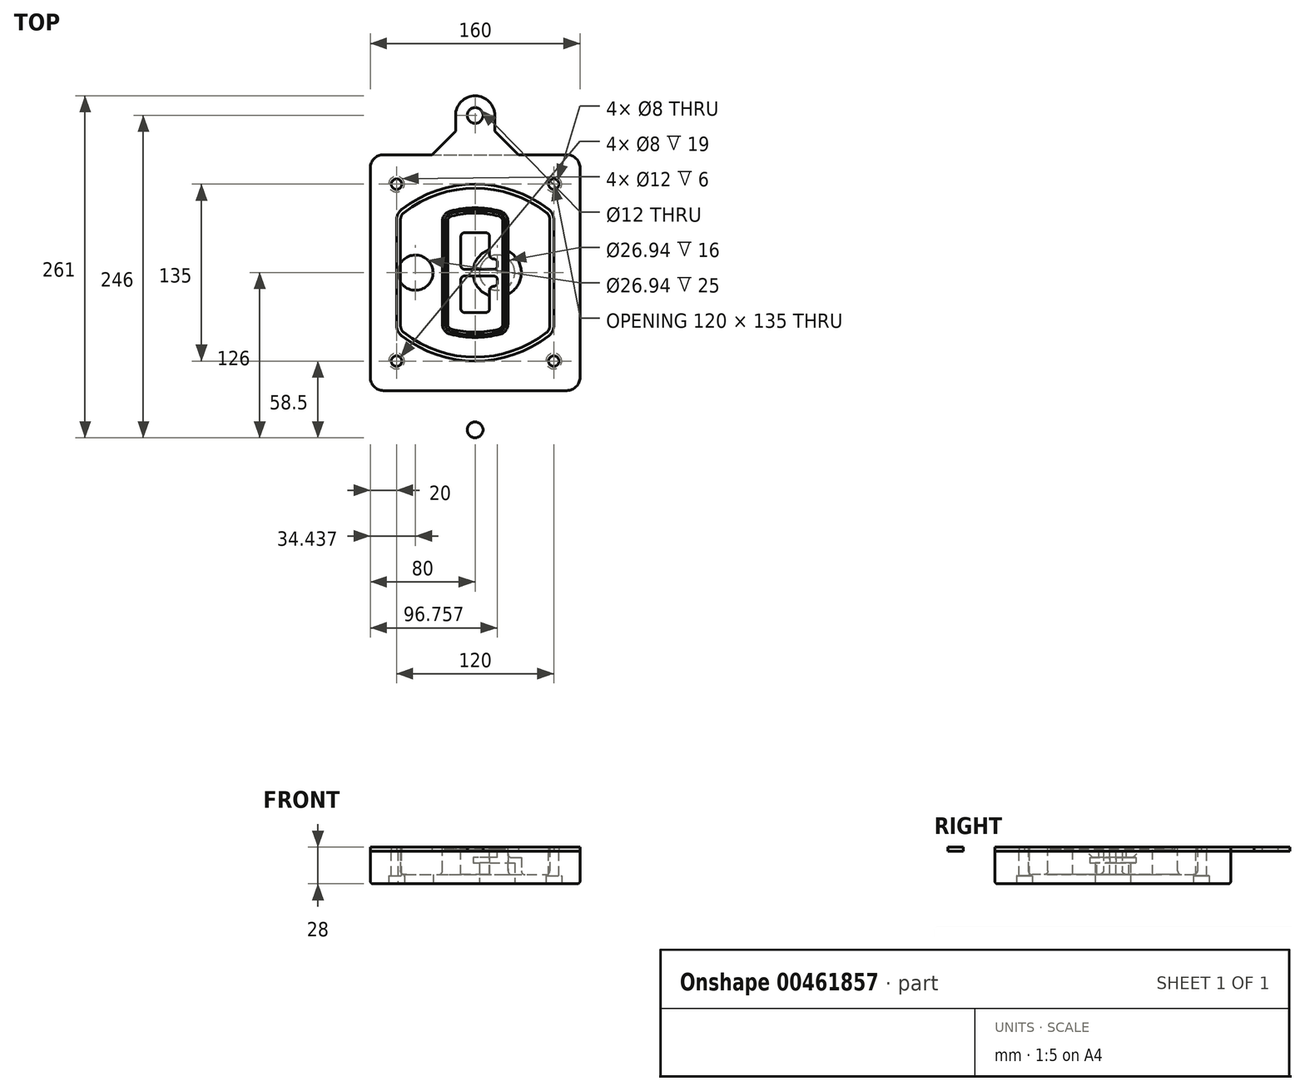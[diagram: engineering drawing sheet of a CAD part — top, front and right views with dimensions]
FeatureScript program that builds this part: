
annotation { "Feature Type Name" : "Feature", "Feature Type Description" : "" }
export const myFeature = defineFeature(function(context is Context, id is Id, definition is map)
    precondition{}
    {
        {
            var Q0;
            Q0=qCreatedBy(makeId("Top.planeOp"),FACE);
            var sketch = newSketch(context, id + "F0", { "sketchPlane" : qUnion([Q0])});
            skPoint(sketch, "E0.rect.middle", {"position": v(0, 0) * mm});
            skLineSegment(sketch, "E1.bottom", {"start": v(-70, -90) * mm, "end": v(70, -90) * mm});
            skLineSegment(sketch, "E1.top", {"start": v(-70, 90) * mm, "end": v(70, 90) * mm});
            skLineSegment(sketch, "E1.left", {"start": v(-80, -80) * mm, "end": v(-80, 80) * mm});
            skLineSegment(sketch, "E1.right", {"start": v(80, -80) * mm, "end": v(80, 80) * mm});
            skLineSegment(sketch, "E2", {"start": v(-80, 90) * mm, "end": v(80, -90) * mm, "construction": true});
            skLineSegment(sketch, "E3", {"start": v(80, 90) * mm, "end": v(-80, -90) * mm, "construction": true});
            skCircle(sketch, "E4", {"center": v(-60, 67.5) * mm, "radius": 4 * mm});
            skCircle(sketch, "E5", {"center": v(60, 67.5) * mm, "radius": 4 * mm});
            skCircle(sketch, "E6", {"center": v(60, -67.5) * mm, "radius": 4 * mm});
            skCircle(sketch, "E7", {"center": v(-60, -67.5) * mm, "radius": 4 * mm});
            skLineSegment(sketch, "E8", {"start": v(-60, 67.5) * mm, "end": v(60, 67.5) * mm, "construction": true});
            skLineSegment(sketch, "E9", {"start": v(60, 67.5) * mm, "end": v(60, -67.5) * mm, "construction": true});
            skLineSegment(sketch, "E10", {"start": v(60, -67.5) * mm, "end": v(-60, -67.5) * mm, "construction": true});
            skLineSegment(sketch, "E11", {"start": v(-60, -67.5) * mm, "end": v(-60, 67.5) * mm, "construction": true});
            skLineSegment(sketch, "E12", {"start": v(-60, 40.3) * mm, "end": v(-60, -40.3) * mm});
            skLineSegment(sketch, "E13", {"start": v(60, 40.3) * mm, "end": v(60, -40.3) * mm});
            skArc(sketch, "E14", {"start": v(56.15, 48.18) * mm, "mid": v(0, 67.5) * mm, "end": v(-56.15, 48.18) * mm});
            skArc(sketch, "E15", {"start": v(-56.15, -48.18) * mm, "mid": v(0, -67.5) * mm, "end": v(56.15, -48.18) * mm});
            skLineSegment(sketch, "E16", {"start": v(-60, 0) * mm, "end": v(60, 0) * mm, "construction": true});
            skPoint(sketch, "E17.visualSharp", {"position": v(-60, -45) * mm});
            skArc(sketch, "E17.filletArc", {"start": v(-60, -40.3) * mm, "mid": v(-58.99, -44.68) * mm, "end": v(-56.15, -48.18) * mm});
            skPoint(sketch, "E18.visualSharp", {"position": v(-60, 45) * mm});
            skArc(sketch, "E18.filletArc", {"start": v(-56.15, 48.18) * mm, "mid": v(-58.99, 44.68) * mm, "end": v(-60, 40.3) * mm});
            skPoint(sketch, "E19.visualSharp", {"position": v(60, 45) * mm});
            skArc(sketch, "E19.filletArc", {"start": v(60, 40.3) * mm, "mid": v(58.99, 44.68) * mm, "end": v(56.15, 48.18) * mm});
            skPoint(sketch, "E20.visualSharp", {"position": v(60, -45) * mm});
            skArc(sketch, "E20.filletArc", {"start": v(56.15, -48.18) * mm, "mid": v(58.99, -44.68) * mm, "end": v(60, -40.3) * mm});
            skPoint(sketch, "E21.visualSharp", {"position": v(-80, 90) * mm});
            skArc(sketch, "E21.filletArc", {"start": v(-70, 90) * mm, "mid": v(-77.07, 87.07) * mm, "end": v(-80, 80) * mm});
            skPoint(sketch, "E22.visualSharp", {"position": v(80, 90) * mm});
            skArc(sketch, "E22.filletArc", {"start": v(80, 80) * mm, "mid": v(77.07, 87.07) * mm, "end": v(70, 90) * mm});
            skPoint(sketch, "E23.visualSharp", {"position": v(80, -90) * mm});
            skArc(sketch, "E23.filletArc", {"start": v(70, -90) * mm, "mid": v(77.07, -87.07) * mm, "end": v(80, -80) * mm});
            skPoint(sketch, "E24.visualSharp", {"position": v(-80, -90) * mm});
            skArc(sketch, "E24.filletArc", {"start": v(-80, -80) * mm, "mid": v(-77.07, -87.07) * mm, "end": v(-70, -90) * mm});
            skArc(sketch, "E25.0", {"start": v(57, 40.3) * mm, "mid": v(56.3, 43.36) * mm, "end": v(54.3, 45.81) * mm});
            skLineSegment(sketch, "E25.1", {"start": v(57, 40.3) * mm, "end": v(57, -40.3) * mm});
            skArc(sketch, "E25.2", {"start": v(54.3, -45.81) * mm, "mid": v(56.3, -43.36) * mm, "end": v(57, -40.3) * mm});
            skArc(sketch, "E25.3", {"start": v(-54.3, -45.81) * mm, "mid": v(0, -64.5) * mm, "end": v(54.3, -45.81) * mm});
            skArc(sketch, "E25.4", {"start": v(-57, -40.3) * mm, "mid": v(-56.3, -43.36) * mm, "end": v(-54.3, -45.81) * mm});
            skArc(sketch, "E25.5", {"start": v(54.3, 45.81) * mm, "mid": v(0, 64.5) * mm, "end": v(-54.3, 45.81) * mm});
            skLineSegment(sketch, "E25.6", {"start": v(-57, 40.3) * mm, "end": v(-57, -40.3) * mm});
            skArc(sketch, "E25.7", {"start": v(-54.3, 45.81) * mm, "mid": v(-56.3, 43.36) * mm, "end": v(-57, 40.3) * mm});
            skArc(sketch, "E26.0", {"start": v(-58.62, 51.33) * mm, "mid": v(-62.58, 46.43) * mm, "end": v(-64, 40.3) * mm});
            skArc(sketch, "E26.1", {"start": v(58.62, 51.33) * mm, "mid": v(0, 71.5) * mm, "end": v(-58.62, 51.33) * mm});
            skArc(sketch, "E26.2", {"start": v(64, 40.3) * mm, "mid": v(62.58, 46.43) * mm, "end": v(58.62, 51.33) * mm});
            skLineSegment(sketch, "E26.3", {"start": v(64, 40.3) * mm, "end": v(64, -40.3) * mm});
            skArc(sketch, "E26.4", {"start": v(58.62, -51.33) * mm, "mid": v(62.58, -46.43) * mm, "end": v(64, -40.3) * mm});
            skLineSegment(sketch, "E26.5", {"start": v(-64, 40.3) * mm, "end": v(-64, -40.3) * mm});
            skArc(sketch, "E26.6", {"start": v(-58.62, -51.33) * mm, "mid": v(0, -71.5) * mm, "end": v(58.62, -51.33) * mm});
            skArc(sketch, "E26.7", {"start": v(-64, -40.3) * mm, "mid": v(-62.58, -46.43) * mm, "end": v(-58.62, -51.33) * mm});
            skSolve(sketch);
        }
        {
            var Q0;
            Q0=makeQuery(id+"F0.imprint","IMPRINT",FACE,{"disambiguationData":[TD([[makeQuery(id+"F0.imprint","IMPRINT",EDGE,{"derivedFrom":sQuery(id+"F0.wireOp",EDGE,"E1.bottom")}),1.0]])]});
            var Q1;
            Q1=makeQuery(id+"F0.imprint","IMPRINT",FACE,{"disambiguationData":[TD([[makeQuery(id+"F0.imprint","IMPRINT",EDGE,{"derivedFrom":sQuery(id+"F0.wireOp",EDGE,"E12")}),1.0]])]});
            var Q2;
            Q2=makeQuery(id+"F0.imprint","IMPRINT",FACE,{"disambiguationData":[TD([[makeQuery(id+"F0.imprint","IMPRINT",EDGE,{"derivedFrom":sQuery(id+"F0.wireOp",EDGE,"E25.0")}),1.0]])]});
            var Q3;
            Q3=makeQuery(id+"F0.imprint","IMPRINT",FACE,{"disambiguationData":[TD([[makeQuery(id+"F0.imprint","IMPRINT",EDGE,{"derivedFrom":sQuery(id+"F0.wireOp",EDGE,"E12")}),-1.0]])]});
            extrude(context, id + "F1", {"entities" : qUnion([Q0, Q1, Q2, Q3]), "oppositeDirection" : true, "depth" : 25 * mm});
        }
        {
            var Q0;
            Q0=makeQuery(id+"F0.imprint","IMPRINT",FACE,{"disambiguationData":[TD([[makeQuery(id+"F0.imprint","IMPRINT",EDGE,{"derivedFrom":sQuery(id+"F0.wireOp",EDGE,"E12")}),1.0]])]});
            extrude(context, id + "F2", {"entities" : qUnion([Q0]), "operationType" : NewBodyOperationType.ADD, "depth" : 3 * mm});
        }
        {
            var Q0;
            Q0=makeQuery(id+"F0.imprint","IMPRINT",FACE,{"disambiguationData":[TD([[makeQuery(id+"F0.imprint","IMPRINT",EDGE,{"derivedFrom":sQuery(id+"F0.wireOp",EDGE,"E25.0")}),1.0]])]});
            extrude(context, id + "F3", {"entities" : qUnion([Q0]), "operationType" : NewBodyOperationType.REMOVE, "oppositeDirection" : true, "depth" : 18 * mm});
        }
        {
            var Q0;
            Q0=makeQuery(id+"F2.opExtrude","CAP_FACE",FACE,{"disambiguationData":[OSD([sQuery(id+"F0.wireOp",EDGE,"E12"),sQuery(id+"F0.wireOp",EDGE,"E13"),sQuery(id+"F0.wireOp",EDGE,"E14"),sQuery(id+"F0.wireOp",EDGE,"E15"),sQuery(id+"F0.wireOp",EDGE,"E17.filletArc"),sQuery(id+"F0.wireOp",EDGE,"E18.filletArc"),sQuery(id+"F0.wireOp",EDGE,"E19.filletArc"),sQuery(id+"F0.wireOp",EDGE,"E20.filletArc"),sQuery(id+"F0.wireOp",EDGE,"E25.0"),sQuery(id+"F0.wireOp",EDGE,"E25.1"),sQuery(id+"F0.wireOp",EDGE,"E25.2"),sQuery(id+"F0.wireOp",EDGE,"E25.3"),sQuery(id+"F0.wireOp",EDGE,"E25.4"),sQuery(id+"F0.wireOp",EDGE,"E25.5"),sQuery(id+"F0.wireOp",EDGE,"E25.6"),sQuery(id+"F0.wireOp",EDGE,"E25.7")])],"isStart":false});
            var sketch = newSketch(context, id + "F4", { "sketchPlane" : qUnion([Q0])});
            skArc(sketch, "E27.0", {"start": v(-19.08, -46.97) * mm, "mid": v(0, -49.5) * mm, "end": v(19.08, -46.97) * mm});
            skArc(sketch, "E28.0", {"start": v(19.08, 46.97) * mm, "mid": v(0, 49.5) * mm, "end": v(-19.08, 46.97) * mm});
            skLineSegment(sketch, "E29", {"start": v(-25, 39.25) * mm, "end": v(-25, -39.25) * mm});
            skLineSegment(sketch, "E30", {"start": v(25, 39.25) * mm, "end": v(25, -39.25) * mm});
            skLineSegment(sketch, "E31", {"start": v(-25, 45.1) * mm, "end": v(25, 45.1) * mm, "construction": true});
            skLineSegment(sketch, "E32", {"start": v(-25, -45.1) * mm, "end": v(25, -45.1) * mm, "construction": true});
            skPoint(sketch, "E33.visualSharp", {"position": v(-25, 45.1) * mm});
            skArc(sketch, "E33.filletArc", {"start": v(-19.08, 46.97) * mm, "mid": v(-23.35, 44.11) * mm, "end": v(-25, 39.25) * mm});
            skPoint(sketch, "E34.visualSharp", {"position": v(25, 45.1) * mm});
            skArc(sketch, "E34.filletArc", {"start": v(25, 39.25) * mm, "mid": v(23.35, 44.11) * mm, "end": v(19.08, 46.97) * mm});
            skPoint(sketch, "E35.visualSharp", {"position": v(25, -45.1) * mm});
            skArc(sketch, "E35.filletArc", {"start": v(19.08, -46.97) * mm, "mid": v(23.35, -44.11) * mm, "end": v(25, -39.25) * mm});
            skPoint(sketch, "E36.visualSharp", {"position": v(-25, -45.1) * mm});
            skArc(sketch, "E36.filletArc", {"start": v(-25, -39.25) * mm, "mid": v(-23.35, -44.11) * mm, "end": v(-19.08, -46.97) * mm});
            skArc(sketch, "E37.0", {"start": v(54.3, 45.81) * mm, "mid": v(0, 64.5) * mm, "end": v(-54.3, 45.81) * mm});
            skArc(sketch, "E37.1", {"start": v(-54.3, 45.81) * mm, "mid": v(-56.3, 43.36) * mm, "end": v(-57, 40.3) * mm});
            skLineSegment(sketch, "E37.2", {"start": v(-57, 40.3) * mm, "end": v(-57, -40.3) * mm});
            skArc(sketch, "E37.3", {"start": v(-57, -40.3) * mm, "mid": v(-56.3, -43.36) * mm, "end": v(-54.3, -45.81) * mm});
            skArc(sketch, "E37.4", {"start": v(-54.3, -45.81) * mm, "mid": v(0, -64.5) * mm, "end": v(54.3, -45.81) * mm});
            skArc(sketch, "E37.5", {"start": v(54.3, -45.81) * mm, "mid": v(56.3, -43.36) * mm, "end": v(57, -40.3) * mm});
            skLineSegment(sketch, "E37.6", {"start": v(57, 40.3) * mm, "end": v(57, -40.3) * mm});
            skArc(sketch, "E37.7", {"start": v(57, 40.3) * mm, "mid": v(56.3, 43.36) * mm, "end": v(54.3, 45.81) * mm});
            skLineSegment(sketch, "E38.0", {"start": v(23, 39.25) * mm, "end": v(23, -39.25) * mm});
            skArc(sketch, "E38.1", {"start": v(18.56, -45.04) * mm, "mid": v(21.76, -42.9) * mm, "end": v(23, -39.25) * mm});
            skArc(sketch, "E38.2", {"start": v(-18.56, -45.04) * mm, "mid": v(0, -47.5) * mm, "end": v(18.56, -45.04) * mm});
            skArc(sketch, "E38.3", {"start": v(-23, -39.25) * mm, "mid": v(-21.76, -42.9) * mm, "end": v(-18.56, -45.04) * mm});
            skLineSegment(sketch, "E38.4", {"start": v(-23, 39.25) * mm, "end": v(-23, -39.25) * mm});
            skArc(sketch, "E38.5", {"start": v(23, 39.25) * mm, "mid": v(21.76, 42.9) * mm, "end": v(18.56, 45.04) * mm});
            skArc(sketch, "E38.6", {"start": v(-18.56, 45.04) * mm, "mid": v(-21.76, 42.9) * mm, "end": v(-23, 39.25) * mm});
            skArc(sketch, "E38.7", {"start": v(18.56, 45.04) * mm, "mid": v(0, 47.5) * mm, "end": v(-18.56, 45.04) * mm});
            skArc(sketch, "E39.0", {"start": v(21, 39.25) * mm, "mid": v(20.18, 41.68) * mm, "end": v(18.04, 43.1) * mm});
            skLineSegment(sketch, "E39.1", {"start": v(21, 39.25) * mm, "end": v(21, -39.25) * mm});
            skArc(sketch, "E39.2", {"start": v(18.04, -43.1) * mm, "mid": v(20.18, -41.68) * mm, "end": v(21, -39.25) * mm});
            skArc(sketch, "E39.3", {"start": v(-18.04, -43.1) * mm, "mid": v(0, -45.5) * mm, "end": v(18.04, -43.1) * mm});
            skArc(sketch, "E39.4", {"start": v(-21, -39.25) * mm, "mid": v(-20.18, -41.68) * mm, "end": v(-18.04, -43.1) * mm});
            skArc(sketch, "E39.5", {"start": v(18.04, 43.1) * mm, "mid": v(0, 45.5) * mm, "end": v(-18.04, 43.1) * mm});
            skLineSegment(sketch, "E39.6", {"start": v(-21, 39.25) * mm, "end": v(-21, -39.25) * mm});
            skArc(sketch, "E39.7", {"start": v(-18.04, 43.1) * mm, "mid": v(-20.18, 41.68) * mm, "end": v(-21, 39.25) * mm});
            skLineSegment(sketch, "E40", {"start": v(-25, 0) * mm, "end": v(25, 0) * mm, "construction": true});
            skLineSegment(sketch, "E41", {"start": v(-11, 5.5) * mm, "end": v(-11, 27.5) * mm});
            skLineSegment(sketch, "E42", {"start": v(-8, 30.5) * mm, "end": v(8, 30.5) * mm});
            skLineSegment(sketch, "E43", {"start": v(11, 27.5) * mm, "end": v(11, 13.5) * mm});
            skLineSegment(sketch, "E44", {"start": v(14, 10.5) * mm, "end": v(14, 10.5) * mm});
            skLineSegment(sketch, "E45", {"start": v(17, 7.5) * mm, "end": v(17, 5.5) * mm});
            skLineSegment(sketch, "E46", {"start": v(14, 2.5) * mm, "end": v(-8, 2.5) * mm});
            skPoint(sketch, "E47.visualSharp", {"position": v(-11, 30.5) * mm});
            skArc(sketch, "E47.filletArc", {"start": v(-8, 30.5) * mm, "mid": v(-10.12, 29.62) * mm, "end": v(-11, 27.5) * mm});
            skPoint(sketch, "E48.visualSharp", {"position": v(11, 30.5) * mm});
            skArc(sketch, "E48.filletArc", {"start": v(11, 27.5) * mm, "mid": v(10.12, 29.62) * mm, "end": v(8, 30.5) * mm});
            skPoint(sketch, "E49.visualSharp", {"position": v(11, 10.5) * mm});
            skArc(sketch, "E49.filletArc", {"start": v(11, 13.5) * mm, "mid": v(11.88, 11.38) * mm, "end": v(14, 10.5) * mm});
            skPoint(sketch, "E50.visualSharp", {"position": v(17, 10.5) * mm});
            skArc(sketch, "E50.filletArc", {"start": v(17, 7.5) * mm, "mid": v(16.12, 9.62) * mm, "end": v(14, 10.5) * mm});
            skPoint(sketch, "E51.visualSharp", {"position": v(17, 2.5) * mm});
            skArc(sketch, "E51.filletArc", {"start": v(14, 2.5) * mm, "mid": v(16.12, 3.38) * mm, "end": v(17, 5.5) * mm});
            skPoint(sketch, "E52.visualSharp", {"position": v(-11, 2.5) * mm});
            skArc(sketch, "E52.filletArc", {"start": v(-11, 5.5) * mm, "mid": v(-10.12, 3.38) * mm, "end": v(-8, 2.5) * mm});
            skLineSegment(sketch, "E53.0.MirrorCS", {"start": v(14, -2.5) * mm, "end": v(-8, -2.5) * mm});
            skArc(sketch, "E54.0.MirrorCS", {"start": v(-11, -5.5) * mm, "mid": v(-10.12, -3.38) * mm, "end": v(-8, -2.5) * mm});
            skLineSegment(sketch, "E55.0.MirrorCS", {"start": v(-11, -5.5) * mm, "end": v(-11, -27.5) * mm});
            skArc(sketch, "E56.0.MirrorCS", {"start": v(-8, -30.5) * mm, "mid": v(-10.12, -29.62) * mm, "end": v(-11, -27.5) * mm});
            skLineSegment(sketch, "E57.0.MirrorCS", {"start": v(-8, -30.5) * mm, "end": v(8, -30.5) * mm});
            skArc(sketch, "E58.0.MirrorCS", {"start": v(11, -27.5) * mm, "mid": v(10.12, -29.62) * mm, "end": v(8, -30.5) * mm});
            skLineSegment(sketch, "E59.0.MirrorCS", {"start": v(11, -27.5) * mm, "end": v(11, -13.5) * mm});
            skArc(sketch, "E60.0.MirrorCS", {"start": v(11, -13.5) * mm, "mid": v(11.88, -11.38) * mm, "end": v(14, -10.5) * mm});
            skArc(sketch, "E61.0.MirrorCS", {"start": v(17, -7.5) * mm, "mid": v(16.12, -9.62) * mm, "end": v(14, -10.5) * mm});
            skLineSegment(sketch, "E62.0.MirrorCS", {"start": v(17, -7.5) * mm, "end": v(17, -5.5) * mm});
            skArc(sketch, "E63.0.MirrorCS", {"start": v(14, -2.5) * mm, "mid": v(16.12, -3.38) * mm, "end": v(17, -5.5) * mm});
            skSolve(sketch);
        }
        {
            var Q0;
            Q0=makeQuery(id+"F4.imprint","IMPRINT",FACE,{"disambiguationData":[TD([[makeQuery(id+"F4.imprint","IMPRINT",EDGE,{"derivedFrom":sQuery(id+"F4.wireOp",EDGE,"E27.0")}),1.0]])]});
            var Q1;
            Q1=makeQuery(id+"F4.imprint","IMPRINT",FACE,{"disambiguationData":[TD([[makeQuery(id+"F4.imprint","IMPRINT",EDGE,{"derivedFrom":sQuery(id+"F4.wireOp",EDGE,"E38.0")}),-1.0]])]});
            var Q2;
            Q2=makeQuery(id+"F4.imprint","IMPRINT",FACE,{"disambiguationData":[TD([[makeQuery(id+"F4.imprint","IMPRINT",EDGE,{"derivedFrom":sQuery(id+"F4.wireOp",EDGE,"E39.0")}),1.0]])]});
            extrude(context, id + "F5", {"entities" : qUnion([Q0, Q1, Q2]), "operationType" : NewBodyOperationType.ADD, "endBound" : BoundingType.UP_TO_NEXT, "oppositeDirection" : true, "depth" : 25 * mm});
        }
        {
            var Q0;
            Q0=makeQuery(id+"F4.imprint","IMPRINT",FACE,{"disambiguationData":[TD([[makeQuery(id+"F4.imprint","IMPRINT",EDGE,{"derivedFrom":sQuery(id+"F4.wireOp",EDGE,"E38.0")}),-1.0]])]});
            extrude(context, id + "F6", {"entities" : qUnion([Q0]), "operationType" : NewBodyOperationType.REMOVE, "oppositeDirection" : true, "depth" : 2 * mm});
        }
        {
            var Q0;
            Q0=makeQuery(id+"F1.opExtrude","CAP_FACE",FACE,{"disambiguationData":[OSD([sQuery(id+"F0.wireOp",EDGE,"E1.bottom"),sQuery(id+"F0.wireOp",EDGE,"E1.top"),sQuery(id+"F0.wireOp",EDGE,"E1.left"),sQuery(id+"F0.wireOp",EDGE,"E1.right"),sQuery(id+"F0.wireOp",EDGE,"E4"),sQuery(id+"F0.wireOp",EDGE,"E5"),sQuery(id+"F0.wireOp",EDGE,"E6"),sQuery(id+"F0.wireOp",EDGE,"E7"),sQuery(id+"F0.wireOp",EDGE,"E21.filletArc"),sQuery(id+"F0.wireOp",EDGE,"E22.filletArc"),sQuery(id+"F0.wireOp",EDGE,"E23.filletArc"),sQuery(id+"F0.wireOp",EDGE,"E24.filletArc")])],"isStart":false});
            var sketch = newSketch(context, id + "F7", { "sketchPlane" : qUnion([Q0])});
            skCircle(sketch, "E64", {"center": v(16.76, 0) * mm, "radius": 13.47 * mm});
            skCircle(sketch, "E65", {"center": v(-45.56, 0) * mm, "radius": 13.47 * mm});
            skLineSegment(sketch, "E66", {"start": v(80, 0) * mm, "end": v(-80, 0) * mm});
            skCircle(sketch, "E67", {"center": v(16.76, 0) * mm, "radius": 18.47 * mm});
            skCircle(sketch, "E68", {"center": v(60, -67.5) * mm, "radius": 6 * mm});
            skCircle(sketch, "E69", {"center": v(-60, -67.5) * mm, "radius": 6 * mm});
            skCircle(sketch, "E70", {"center": v(-60, 67.5) * mm, "radius": 6 * mm});
            skCircle(sketch, "E71", {"center": v(60, 67.5) * mm, "radius": 6 * mm});
            skSolve(sketch);
        }
        {
            var Q0;
            {var subQ1=sQuery(id+"F7.wireOp",EDGE,"E66");var subQ4=sQuery(id+"F7.wireOp",EDGE,"E64");var subQ6=makeQuery(id+"F7.imprint","INTERSECT",VERTEX,{"disambiguationData":[OD(0.0)],"derivedFrom":[subQ4,subQ1]});Q0=makeQuery(id+"F7.imprint","IMPRINT",FACE,{"disambiguationData":[TD([[makeQuery(id+"F7.imprint","IMPRINT",EDGE,{"disambiguationData":[TD([[subQ6,-1.0]])],"derivedFrom":subQ4}),-1.0]])]});}
            var Q1;
            {var subQ0=sQuery(id+"F7.wireOp",EDGE,"E66");var subQ1=sQuery(id+"F7.wireOp",EDGE,"E64");var subQ3=makeQuery(id+"F7.imprint","INTERSECT",VERTEX,{"disambiguationData":[OD(0.0)],"derivedFrom":[subQ1,subQ0]});Q1=makeQuery(id+"F7.imprint","IMPRINT",FACE,{"disambiguationData":[TD([[makeQuery(id+"F7.imprint","IMPRINT",EDGE,{"disambiguationData":[TD([[subQ3,-1.0]])],"derivedFrom":subQ1}),1.0]])]});}
            var Q2;
            {var subQ0=sQuery(id+"F7.wireOp",EDGE,"E66");var subQ1=sQuery(id+"F7.wireOp",EDGE,"E64");var subQ3=makeQuery(id+"F7.imprint","INTERSECT",VERTEX,{"disambiguationData":[OD(0.0)],"derivedFrom":[subQ1,subQ0]});Q2=makeQuery(id+"F7.imprint","IMPRINT",FACE,{"disambiguationData":[TD([[makeQuery(id+"F7.imprint","IMPRINT",EDGE,{"disambiguationData":[TD([[subQ3,1.0]])],"derivedFrom":subQ1}),1.0]])]});}
            var Q3;
            {var subQ1=sQuery(id+"F7.wireOp",EDGE,"E66");var subQ4=sQuery(id+"F7.wireOp",EDGE,"E64");var subQ6=makeQuery(id+"F7.imprint","INTERSECT",VERTEX,{"disambiguationData":[OD(0.0)],"derivedFrom":[subQ4,subQ1]});Q3=makeQuery(id+"F7.imprint","IMPRINT",FACE,{"disambiguationData":[TD([[makeQuery(id+"F7.imprint","IMPRINT",EDGE,{"disambiguationData":[TD([[subQ6,1.0]])],"derivedFrom":subQ4}),-1.0]])]});}
            extrude(context, id + "F8", {"entities" : qUnion([Q0, Q1, Q2, Q3]), "operationType" : NewBodyOperationType.ADD, "oppositeDirection" : true, "depth" : 20 * mm});
        }
        {
            var Q0;
            {var subQ0=sQuery(id+"F7.wireOp",EDGE,"E66");var subQ1=sQuery(id+"F7.wireOp",EDGE,"E64");var subQ3=makeQuery(id+"F7.imprint","INTERSECT",VERTEX,{"disambiguationData":[OD(0.0)],"derivedFrom":[subQ1,subQ0]});Q0=makeQuery(id+"F7.imprint","IMPRINT",FACE,{"disambiguationData":[TD([[makeQuery(id+"F7.imprint","IMPRINT",EDGE,{"disambiguationData":[TD([[subQ3,-1.0]])],"derivedFrom":subQ1}),1.0]])]});}
            var Q1;
            {var subQ0=sQuery(id+"F7.wireOp",EDGE,"E66");var subQ1=sQuery(id+"F7.wireOp",EDGE,"E64");var subQ3=makeQuery(id+"F7.imprint","INTERSECT",VERTEX,{"disambiguationData":[OD(0.0)],"derivedFrom":[subQ1,subQ0]});Q1=makeQuery(id+"F7.imprint","IMPRINT",FACE,{"disambiguationData":[TD([[makeQuery(id+"F7.imprint","IMPRINT",EDGE,{"disambiguationData":[TD([[subQ3,1.0]])],"derivedFrom":subQ1}),1.0]])]});}
            extrude(context, id + "F9", {"entities" : qUnion([Q0, Q1]), "operationType" : NewBodyOperationType.REMOVE, "oppositeDirection" : true, "depth" : 16 * mm});
        }
        {
            var Q0;
            {var subQ0=sQuery(id+"F7.wireOp",EDGE,"E66");var subQ1=sQuery(id+"F7.wireOp",EDGE,"E65");var subQ3=makeQuery(id+"F7.imprint","INTERSECT",VERTEX,{"disambiguationData":[OD(0.0)],"derivedFrom":[subQ1,subQ0]});Q0=makeQuery(id+"F7.imprint","IMPRINT",FACE,{"disambiguationData":[TD([[makeQuery(id+"F7.imprint","IMPRINT",EDGE,{"disambiguationData":[TD([[subQ3,-1.0]])],"derivedFrom":subQ1}),1.0]])]});}
            var Q1;
            {var subQ0=sQuery(id+"F7.wireOp",EDGE,"E66");var subQ1=sQuery(id+"F7.wireOp",EDGE,"E65");var subQ3=makeQuery(id+"F7.imprint","INTERSECT",VERTEX,{"disambiguationData":[OD(0.0)],"derivedFrom":[subQ1,subQ0]});Q1=makeQuery(id+"F7.imprint","IMPRINT",FACE,{"disambiguationData":[TD([[makeQuery(id+"F7.imprint","IMPRINT",EDGE,{"disambiguationData":[TD([[subQ3,1.0]])],"derivedFrom":subQ1}),1.0]])]});}
            extrude(context, id + "F10", {"entities" : qUnion([Q0, Q1]), "operationType" : NewBodyOperationType.REMOVE, "oppositeDirection" : true, "depth" : 25 * mm});
        }
        {
            var Q0;
            Q0=makeQuery(id+"F7.imprint","IMPRINT",FACE,{"disambiguationData":[TD([[makeQuery(id+"F7.imprint","IMPRINT",EDGE,{"derivedFrom":sQuery(id+"F7.wireOp",EDGE,"E68")}),1.0]])]});
            var Q1;
            Q1=makeQuery(id+"F7.imprint","IMPRINT",FACE,{"disambiguationData":[TD([[makeQuery(id+"F7.imprint","IMPRINT",EDGE,{"derivedFrom":makeQuery(id+"F1.opExtrude","CAP_EDGE",EDGE,{"disambiguationData":[OSD([sQuery(id+"F0.wireOp",EDGE,"E5")])],"isStart":false})}),-1.0]])]});
            var Q2;
            Q2=makeQuery(id+"F7.imprint","IMPRINT",FACE,{"disambiguationData":[TD([[makeQuery(id+"F7.imprint","IMPRINT",EDGE,{"derivedFrom":sQuery(id+"F7.wireOp",EDGE,"E69")}),1.0]])]});
            var Q3;
            Q3=makeQuery(id+"F7.imprint","IMPRINT",FACE,{"disambiguationData":[TD([[makeQuery(id+"F7.imprint","IMPRINT",EDGE,{"derivedFrom":makeQuery(id+"F1.opExtrude","CAP_EDGE",EDGE,{"disambiguationData":[OSD([sQuery(id+"F0.wireOp",EDGE,"E4")])],"isStart":false})}),-1.0]])]});
            var Q4;
            Q4=makeQuery(id+"F7.imprint","IMPRINT",FACE,{"disambiguationData":[TD([[makeQuery(id+"F7.imprint","IMPRINT",EDGE,{"derivedFrom":sQuery(id+"F7.wireOp",EDGE,"E70")}),1.0]])]});
            var Q5;
            Q5=makeQuery(id+"F7.imprint","IMPRINT",FACE,{"disambiguationData":[TD([[makeQuery(id+"F7.imprint","IMPRINT",EDGE,{"derivedFrom":makeQuery(id+"F1.opExtrude","CAP_EDGE",EDGE,{"disambiguationData":[OSD([sQuery(id+"F0.wireOp",EDGE,"E7")])],"isStart":false})}),-1.0]])]});
            var Q6;
            Q6=makeQuery(id+"F7.imprint","IMPRINT",FACE,{"disambiguationData":[TD([[makeQuery(id+"F7.imprint","IMPRINT",EDGE,{"derivedFrom":sQuery(id+"F7.wireOp",EDGE,"E71")}),1.0]])]});
            var Q7;
            Q7=makeQuery(id+"F7.imprint","IMPRINT",FACE,{"disambiguationData":[TD([[makeQuery(id+"F7.imprint","IMPRINT",EDGE,{"derivedFrom":makeQuery(id+"F1.opExtrude","CAP_EDGE",EDGE,{"disambiguationData":[OSD([sQuery(id+"F0.wireOp",EDGE,"E6")])],"isStart":false})}),-1.0]])]});
            extrude(context, id + "F11", {"entities" : qUnion([Q0, Q1, Q2, Q3, Q4, Q5, Q6, Q7]), "operationType" : NewBodyOperationType.REMOVE, "oppositeDirection" : true, "depth" : 6 * mm});
        }
        {
            var Q0;
            Q0=makeQuery(id+"F9.boolean.opBoolean","COPY",FACE,{"derivedFrom":makeQuery(id+"F9.opExtrude","CAP_FACE",FACE,{"disambiguationData":[OSD([sQuery(id+"F7.wireOp",EDGE,"E64")])],"isStart":false})});
            var sketch = newSketch(context, id + "F12", { "sketchPlane" : qUnion([Q0])});
            skArc(sketch, "E72.0", {"start": v(11, 17.55) * mm, "mid": v(2.57, 11.82) * mm, "end": v(-1.54, 2.5) * mm});
            skArc(sketch, "E72.1", {"start": v(-1.54, -2.5) * mm, "mid": v(2.57, -11.82) * mm, "end": v(11, -17.55) * mm});
            skLineSegment(sketch, "E73", {"start": v(-1.54, -2.5) * mm, "end": v(14, -2.5) * mm});
            skLineSegment(sketch, "E74.0", {"start": v(14, 2.5) * mm, "end": v(-1.54, 2.5) * mm});
            skArc(sketch, "E74.1", {"start": v(14, 2.5) * mm, "mid": v(16.12, 3.38) * mm, "end": v(17, 5.5) * mm});
            skLineSegment(sketch, "E74.2", {"start": v(17, 7.5) * mm, "end": v(17, 5.5) * mm});
            skArc(sketch, "E74.3", {"start": v(17, 7.5) * mm, "mid": v(16.12, 9.62) * mm, "end": v(14, 10.5) * mm});
            skArc(sketch, "E74.4", {"start": v(11, 13.5) * mm, "mid": v(11.88, 11.38) * mm, "end": v(14, 10.5) * mm});
            skLineSegment(sketch, "E74.5", {"start": v(11, 17.55) * mm, "end": v(11, 13.5) * mm});
            skLineSegment(sketch, "E74.7", {"start": v(14, -2.5) * mm, "end": v(-1.54, -2.5) * mm});
            skArc(sketch, "E74.8", {"start": v(14, -2.5) * mm, "mid": v(16.12, -3.38) * mm, "end": v(17, -5.5) * mm});
            skLineSegment(sketch, "E74.9", {"start": v(17, -7.5) * mm, "end": v(17, -5.5) * mm});
            skArc(sketch, "E74.10", {"start": v(17, -7.5) * mm, "mid": v(16.12, -9.62) * mm, "end": v(14, -10.5) * mm});
            skArc(sketch, "E74.11", {"start": v(11, -13.5) * mm, "mid": v(11.88, -11.38) * mm, "end": v(14, -10.5) * mm});
            skLineSegment(sketch, "E74.12", {"start": v(11, -17.55) * mm, "end": v(11, -13.5) * mm});
            skPoint(sketch, "E75.orphan", {"position": v(11, -27.5) * mm});
            skPoint(sketch, "E76.orphan", {"position": v(-8, -2.5) * mm});
            skPoint(sketch, "E77.orphan", {"position": v(-8, 2.5) * mm});
            skPoint(sketch, "E78.orphan", {"position": v(11, 27.5) * mm});
            skSolve(sketch);
        }
        {
            var Q0;
            {var subQ7=sQuery(id+"F12.wireOp",EDGE,"E72.0");var subQ14=sQuery(id+"F12.wireOp",EDGE,"E72.1");var subQ16=sQuery(id+"F12.wireOp",EDGE,"E74.1");var subQ18=sQuery(id+"F12.wireOp",EDGE,"E74.8");Q0=qUnion([makeQuery(id+"F12.imprint","IMPRINT",FACE,{"disambiguationData":[TD([[makeQuery(id+"F12.imprint","IMPRINT",EDGE,{"derivedFrom":subQ7}),1.0]])]}),makeQuery(id+"F12.imprint","IMPRINT",FACE,{"disambiguationData":[TD([[makeQuery(id+"F12.imprint","IMPRINT",EDGE,{"derivedFrom":subQ14}),1.0]])]}),makeQuery(id+"F12.imprint","IMPRINT",FACE,{"disambiguationData":[TD([[makeQuery(id+"F12.imprint","IMPRINT",EDGE,{"derivedFrom":subQ16}),1.0]])]}),makeQuery(id+"F12.imprint","IMPRINT",FACE,{"disambiguationData":[TD([[makeQuery(id+"F12.imprint","IMPRINT",EDGE,{"derivedFrom":subQ18}),-1.0]])]})]);}
            var Q1;
            Q1=makeQuery(id+"F5.boolean.opBoolean","SPLIT",FACE,{"disambiguationData":[TD([makeQuery(id+"F5.opExtrude","SWEPT_FACE",FACE,{"disambiguationData":[OSD([sQuery(id+"F4.wireOp",EDGE,"E41")])]})])],"derivedFrom":makeQuery(id+"F3.boolean.opBoolean","COPY",FACE,{"derivedFrom":makeQuery(id+"F3.opExtrude","CAP_FACE",FACE,{"disambiguationData":[OSD([sQuery(id+"F0.wireOp",EDGE,"E25.0"),sQuery(id+"F0.wireOp",EDGE,"E25.1"),sQuery(id+"F0.wireOp",EDGE,"E25.2"),sQuery(id+"F0.wireOp",EDGE,"E25.3"),sQuery(id+"F0.wireOp",EDGE,"E25.4"),sQuery(id+"F0.wireOp",EDGE,"E25.5"),sQuery(id+"F0.wireOp",EDGE,"E25.6"),sQuery(id+"F0.wireOp",EDGE,"E25.7")])],"isStart":false})})});
            extrude(context, id + "F13", {"entities" : qUnion([Q0]), "operationType" : NewBodyOperationType.REMOVE, "endBound" : BoundingType.UP_TO_SURFACE, "endBoundEntityFace" : qUnion([Q1]), "depth" : 25 * mm});
        }
        {
            var Q0;
            Q0=makeQuery(id+"F3.boolean.opBoolean","COPY",EDGE,{"derivedFrom":makeQuery(id+"F3.opExtrude","CAP_EDGE",EDGE,{"disambiguationData":[OSD([sQuery(id+"F0.wireOp",EDGE,"E25.6")])],"isStart":false})});
            var Q1;
            Q1=makeQuery(id+"F8.boolean.opBoolean","INTERSECT",EDGE,{"derivedFrom":[makeQuery(id+"F5.opExtrude","SWEPT_FACE",FACE,{"disambiguationData":[OSD([sQuery(id+"F4.wireOp",EDGE,"E30")])]}),makeQuery(id+"F8.opExtrude","CAP_FACE",FACE,{"disambiguationData":[OSD([sQuery(id+"F7.wireOp",EDGE,"E67")])],"isStart":false})]});
            var Q2;
            Q2=makeQuery(id+"F8.boolean.opBoolean","INTERSECT",EDGE,{"disambiguationData":[OD(1.0)],"derivedFrom":[makeQuery(id+"F5.opExtrude","SWEPT_FACE",FACE,{"disambiguationData":[OSD([sQuery(id+"F4.wireOp",EDGE,"E30")])]}),makeQuery(id+"F8.opExtrude","SWEPT_FACE",FACE,{"disambiguationData":[OSD([sQuery(id+"F7.wireOp",EDGE,"E67")])]})]});
            var Q3;
            {var subQ0=sQuery(id+"F4.wireOp",EDGE,"E30");Q3=makeQuery(id+"F8.boolean.opBoolean","SPLIT",EDGE,{"disambiguationData":[TD([makeQuery(id+"F5.opExtrude","SWEPT_FACE",FACE,{"disambiguationData":[OSD([sQuery(id+"F4.wireOp",EDGE,"E35.filletArc")])]})])],"derivedFrom":makeQuery(id+"F5.opExtrude","CAP_EDGE",EDGE,{"disambiguationData":[OSD([subQ0])],"isStart":false})});}
            var Q4;
            {var subQ0=sQuery(id+"F0.wireOp",EDGE,"E25.7");var subQ1=sQuery(id+"F0.wireOp",EDGE,"E25.1");var subQ2=sQuery(id+"F0.wireOp",EDGE,"E25.6");var subQ3=sQuery(id+"F0.wireOp",EDGE,"E25.5");var subQ4=sQuery(id+"F0.wireOp",EDGE,"E25.4");var subQ5=sQuery(id+"F0.wireOp",EDGE,"E25.0");var subQ6=sQuery(id+"F0.wireOp",EDGE,"E25.2");var subQ7=sQuery(id+"F0.wireOp",EDGE,"E25.3");Q4=makeQuery(id+"F8.boolean.opBoolean","INTERSECT",EDGE,{"derivedFrom":[makeQuery(id+"F5.boolean.opBoolean","SPLIT",FACE,{"disambiguationData":[TD([makeQuery(id+"F2.opExtrude","SWEPT_FACE",FACE,{"disambiguationData":[OSD([subQ5])]})])],"derivedFrom":makeQuery(id+"F3.boolean.opBoolean","COPY",FACE,{"derivedFrom":makeQuery(id+"F3.opExtrude","CAP_FACE",FACE,{"disambiguationData":[OSD([subQ5,subQ1,subQ6,subQ7,subQ4,subQ3,subQ2,subQ0])],"isStart":false})})}),makeQuery(id+"F8.opExtrude","SWEPT_FACE",FACE,{"disambiguationData":[OSD([sQuery(id+"F7.wireOp",EDGE,"E67")])]})]});}
            var Q5;
            Q5=makeQuery(id+"F8.boolean.opBoolean","INTERSECT",EDGE,{"disambiguationData":[OD(0.0)],"derivedFrom":[makeQuery(id+"F5.opExtrude","SWEPT_FACE",FACE,{"disambiguationData":[OSD([sQuery(id+"F4.wireOp",EDGE,"E30")])]}),makeQuery(id+"F8.opExtrude","SWEPT_FACE",FACE,{"disambiguationData":[OSD([sQuery(id+"F7.wireOp",EDGE,"E67")])]})]});
            fillet(context, id + "F14", {"entities" : qUnion([Q0, Q1, Q2, Q3, Q4, Q5]), "radius" : 3 * mm, "tangentPropagation" : true, "allowEdgeOverflow" : false});
        }
        {
            var Q0;
            Q0=makeQuery(id+"F1.opExtrude","CAP_EDGE",EDGE,{"disambiguationData":[OSD([sQuery(id+"F0.wireOp",EDGE,"E1.bottom")])],"isStart":false});
            fillet(context, id + "F15", {"entities" : qUnion([Q0]), "radius" : 2 * mm, "tangentPropagation" : true, "allowEdgeOverflow" : false});
        }
        {
            var Q0;
            {var subQ0=sQuery(id+"F0.wireOp",EDGE,"E21.filletArc");var subQ1=sQuery(id+"F0.wireOp",EDGE,"E7");var subQ2=sQuery(id+"F0.wireOp",EDGE,"E6");var subQ3=sQuery(id+"F0.wireOp",EDGE,"E5");var subQ4=sQuery(id+"F0.wireOp",EDGE,"E4");var subQ5=sQuery(id+"F0.wireOp",EDGE,"E22.filletArc");var subQ6=sQuery(id+"F0.wireOp",EDGE,"E1.bottom");var subQ7=sQuery(id+"F0.wireOp",EDGE,"E1.right");var subQ8=sQuery(id+"F0.wireOp",EDGE,"E1.top");var subQ9=sQuery(id+"F0.wireOp",EDGE,"E1.left");var subQ10=sQuery(id+"F0.wireOp",EDGE,"E23.filletArc");var subQ11=sQuery(id+"F0.wireOp",EDGE,"E24.filletArc");Q0=makeQuery(id+"F2.boolean.opBoolean","SPLIT",FACE,{"disambiguationData":[TD([makeQuery(id+"F1.opExtrude","SWEPT_FACE",FACE,{"disambiguationData":[OSD([subQ6])]})])],"derivedFrom":makeQuery(id+"F1.opExtrude","CAP_FACE",FACE,{"disambiguationData":[OSD([subQ6,subQ8,subQ9,subQ7,subQ4,subQ3,subQ2,subQ1,subQ0,subQ5,subQ10,subQ11])],"isStart":true})});}
            var sketch = newSketch(context, id + "F16", { "sketchPlane" : qUnion([Q0])});
            skPoint(sketch, "E79.endSnap0", {"position": v(0, -90) * mm});
            skLineSegment(sketch, "E80", {"start": v(0, 90) * mm, "end": v(0, 120) * mm, "construction": true});
            skPoint(sketch, "E80.endSnap0", {"position": v(0, 90) * mm});
            skCircle(sketch, "E81", {"center": v(0, 120) * mm, "radius": 6 * mm});
            skLineSegment(sketch, "E82", {"start": v(-15, 108) * mm, "end": v(-15, 120) * mm});
            skLineSegment(sketch, "E83", {"start": v(15, 108) * mm, "end": v(15, 120) * mm});
            skArc(sketch, "E84", {"start": v(15, 120) * mm, "mid": v(0, 135) * mm, "end": v(-15, 120) * mm});
            skLineSegment(sketch, "E85", {"start": v(-15, 108) * mm, "end": v(-33, 90) * mm});
            skLineSegment(sketch, "E86", {"start": v(15, 108) * mm, "end": v(33, 90) * mm});
            skLineSegment(sketch, "E87", {"start": v(-80, 0) * mm, "end": v(80, 0) * mm, "construction": true});
            skLineSegment(sketch, "E88.MirrorCS", {"start": v(15, -108) * mm, "end": v(33, -90) * mm});
            skCircle(sketch, "E89.MirrorC", {"center": v(0, -120) * mm, "radius": 6 * mm});
            skLineSegment(sketch, "E90.MirrorCS", {"start": v(15, -108) * mm, "end": v(15, -120) * mm});
            skLineSegment(sketch, "E91.MirrorCS", {"start": v(-15, -108) * mm, "end": v(-33, -90) * mm});
            skLineSegment(sketch, "E92.MirrorCS", {"start": v(0, -90) * mm, "end": v(0, -120) * mm, "construction": true});
            skLineSegment(sketch, "E93.MirrorCS", {"start": v(-15, -108) * mm, "end": v(-15, -120) * mm});
            skArc(sketch, "E94.MirrorCS", {"start": v(15, -120) * mm, "mid": v(0, -135) * mm, "end": v(-15, -120) * mm});
            skSolve(sketch);
        }
        {
            var Q0;
            Q0=makeQuery(id+"F16.imprint","IMPRINT",FACE,{"disambiguationData":[TD([[makeQuery(id+"F16.imprint","IMPRINT",EDGE,{"derivedFrom":makeQuery(id+"F1.opExtrude","CAP_EDGE",EDGE,{"disambiguationData":[OSD([sQuery(id+"F0.wireOp",EDGE,"E1.left")])],"isStart":true})}),-1.0]])]});
            var Q1;
            Q1=makeQuery(id+"F16.imprint","IMPRINT",FACE,{"disambiguationData":[TD([[makeQuery(id+"F16.imprint","IMPRINT",EDGE,{"derivedFrom":sQuery(id+"F16.wireOp",EDGE,"E81")}),-1.0]])]});
            var Q2;
            Q2=makeQuery(id+"F16.imprint","IMPRINT",FACE,{"disambiguationData":[TD([[makeQuery(id+"F16.imprint","IMPRINT",EDGE,{"derivedFrom":sQuery(id+"F16.wireOp",EDGE,"E89.MirrorC")}),1.0]])]});
            var Q3;
            Q3=makeQuery(id+"F2.opExtrude","CAP_FACE",FACE,{"disambiguationData":[OSD([sQuery(id+"F0.wireOp",EDGE,"E12"),sQuery(id+"F0.wireOp",EDGE,"E13"),sQuery(id+"F0.wireOp",EDGE,"E14"),sQuery(id+"F0.wireOp",EDGE,"E15"),sQuery(id+"F0.wireOp",EDGE,"E17.filletArc"),sQuery(id+"F0.wireOp",EDGE,"E18.filletArc"),sQuery(id+"F0.wireOp",EDGE,"E19.filletArc"),sQuery(id+"F0.wireOp",EDGE,"E20.filletArc"),sQuery(id+"F0.wireOp",EDGE,"E25.0"),sQuery(id+"F0.wireOp",EDGE,"E25.1"),sQuery(id+"F0.wireOp",EDGE,"E25.2"),sQuery(id+"F0.wireOp",EDGE,"E25.3"),sQuery(id+"F0.wireOp",EDGE,"E25.4"),sQuery(id+"F0.wireOp",EDGE,"E25.5"),sQuery(id+"F0.wireOp",EDGE,"E25.6"),sQuery(id+"F0.wireOp",EDGE,"E25.7")])],"isStart":false});
            extrude(context, id + "F17", {"entities" : qUnion([Q0, Q1, Q2]), "endBound" : BoundingType.UP_TO_SURFACE, "endBoundEntityFace" : qUnion([Q3]), "depth" : 25 * mm});
        }
    });
